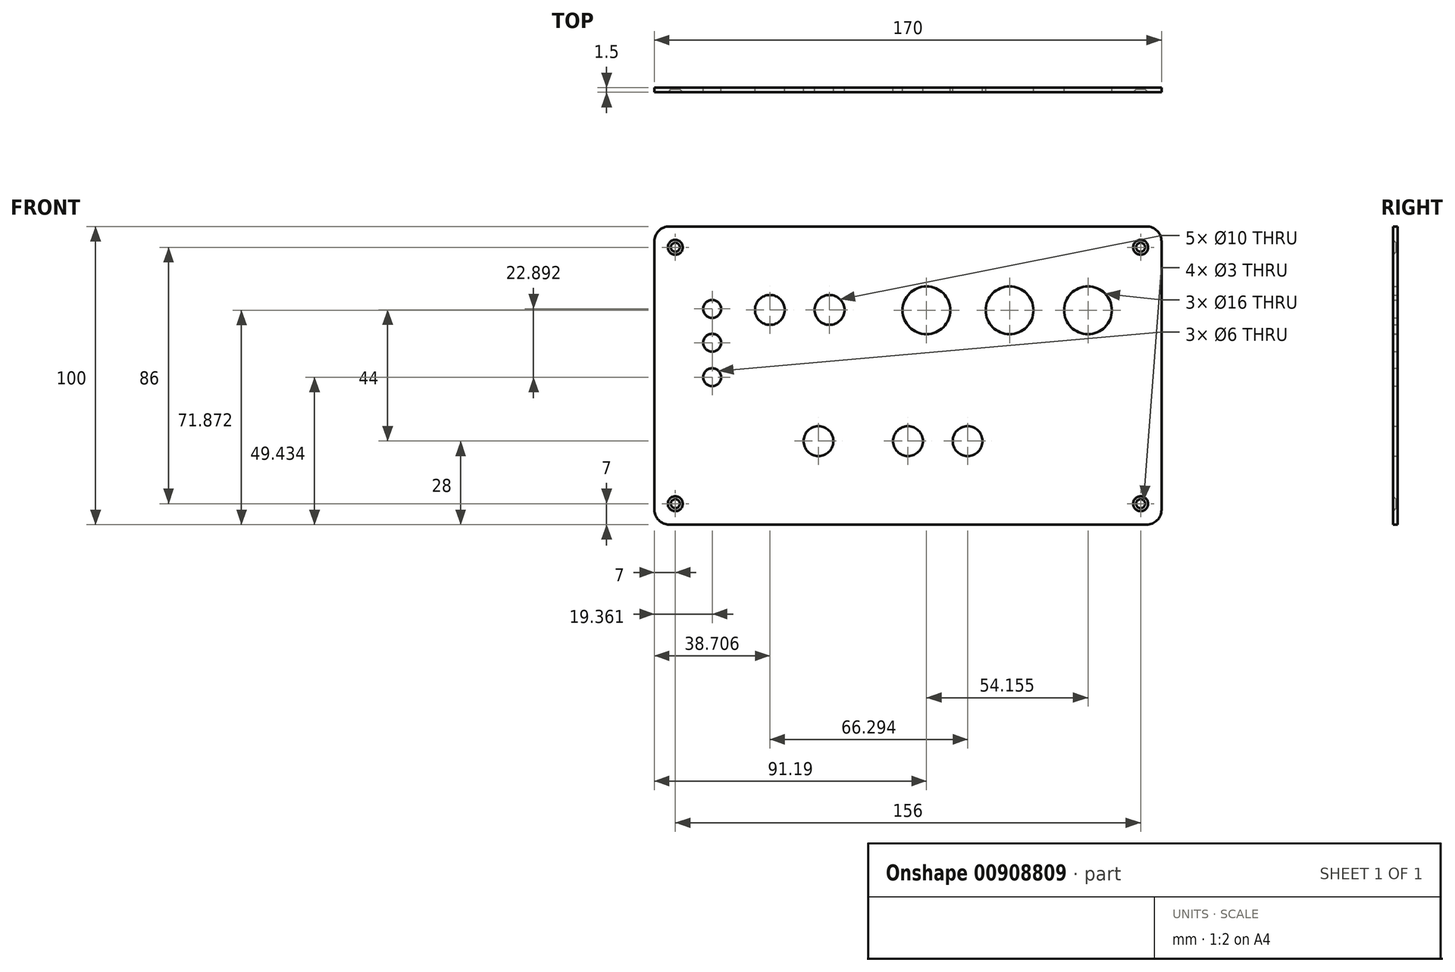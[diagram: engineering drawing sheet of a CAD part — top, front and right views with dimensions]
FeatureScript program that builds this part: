
annotation { "Feature Type Name" : "Feature", "Feature Type Description" : "" }
export const myFeature = defineFeature(function(context is Context, id is Id, definition is map)
    precondition{}
    {
        {
            var Q0;
            Q0=qCreatedBy(makeId("Front.planeOp"),FACE);
            var sketch = newSketch(context, id + "F0", { "sketchPlane" : qUnion([Q0])});
            skLineSegment(sketch, "E0.bottom", {"start": v(5, 0) * mm, "end": v(165, 0) * mm});
            skLineSegment(sketch, "E0.top", {"start": v(5, 100) * mm, "end": v(165, 100) * mm});
            skLineSegment(sketch, "E0.left", {"start": v(0, 5) * mm, "end": v(0, 95) * mm});
            skLineSegment(sketch, "E0.right", {"start": v(170, 5) * mm, "end": v(170, 95) * mm});
            skCircle(sketch, "E1", {"center": v(145.35, 71.87) * mm, "radius": 8 * mm});
            skPoint(sketch, "E2.visualSharp", {"position": v(0, 100) * mm});
            skArc(sketch, "E2.filletArc", {"start": v(5, 100) * mm, "mid": v(1.46, 98.54) * mm, "end": v(0, 95) * mm});
            skPoint(sketch, "E3.visualSharp", {"position": v(0, 0) * mm});
            skArc(sketch, "E3.filletArc", {"start": v(0, 5) * mm, "mid": v(1.46, 1.46) * mm, "end": v(5, 0) * mm});
            skPoint(sketch, "E4.visualSharp", {"position": v(170, 0) * mm});
            skArc(sketch, "E4.filletArc", {"start": v(165, 0) * mm, "mid": v(168.54, 1.46) * mm, "end": v(170, 5) * mm});
            skPoint(sketch, "E5.visualSharp", {"position": v(170, 100) * mm});
            skArc(sketch, "E5.filletArc", {"start": v(170, 95) * mm, "mid": v(168.54, 98.54) * mm, "end": v(165, 100) * mm});
            skLineSegment(sketch, "E6.bottom", {"start": v(163, 7) * mm, "end": v(7, 7) * mm, "construction": true});
            skLineSegment(sketch, "E6.top", {"start": v(163, 93) * mm, "end": v(7, 93) * mm, "construction": true});
            skLineSegment(sketch, "E6.left", {"start": v(163, 7) * mm, "end": v(163, 93) * mm, "construction": true});
            skLineSegment(sketch, "E6.right", {"start": v(7, 7) * mm, "end": v(7, 93) * mm, "construction": true});
            skCircle(sketch, "E7", {"center": v(7, 7) * mm, "radius": 1.5 * mm});
            skCircle(sketch, "E8", {"center": v(163, 93) * mm, "radius": 1.5 * mm});
            skCircle(sketch, "E9", {"center": v(163, 7) * mm, "radius": 1.5 * mm});
            skCircle(sketch, "E10", {"center": v(7, 93) * mm, "radius": 1.5 * mm});
            skCircle(sketch, "E11", {"center": v(105, 28) * mm, "radius": 5 * mm});
            skCircle(sketch, "E12", {"center": v(91.2, 71.87) * mm, "radius": 8 * mm});
            skCircle(sketch, "E13", {"center": v(85, 28) * mm, "radius": 5 * mm});
            skCircle(sketch, "E14", {"center": v(119.06, 71.87) * mm, "radius": 8 * mm});
            skCircle(sketch, "E15", {"center": v(55, 28) * mm, "radius": 5 * mm});
            skLineSegment(sketch, "E16", {"start": v(12.83, 28) * mm, "end": v(149.09, 28) * mm, "construction": true});
            skPoint(sketch, "E17", {"position": v(85, 0) * mm});
            skPoint(sketch, "E18", {"position": v(85, 100) * mm});
            skCircle(sketch, "E19", {"center": v(19.36, 49.43) * mm, "radius": 3 * mm});
            skCircle(sketch, "E20", {"center": v(38.7, 72) * mm, "radius": 5 * mm});
            skCircle(sketch, "E21", {"center": v(58.7, 72) * mm, "radius": 5 * mm});
            skCircle(sketch, "E22", {"center": v(19.36, 61) * mm, "radius": 3 * mm});
            skLineSegment(sketch, "E23", {"start": v(38.7, 72) * mm, "end": v(58.7, 72) * mm, "construction": true});
            skCircle(sketch, "E24", {"center": v(19.36, 72.33) * mm, "radius": 3 * mm});
            skSolve(sketch);
        }
        {
            var Q0;
            Q0=qSketchRegion(id+"F0",true);
            extrude(context, id + "F1", {"entities" : qUnion([Q0]), "depth" : 1.5 * mm});
        }
        {
            var Q0;
            Q0=makeQuery(id+"F1.opExtrude","CAP_EDGE",EDGE,{"disambiguationData":[OSD([sQuery(id+"F0.wireOp",EDGE,"E8")])],"isStart":false});
            var Q1;
            Q1=makeQuery(id+"F1.opExtrude","CAP_EDGE",EDGE,{"disambiguationData":[OSD([sQuery(id+"F0.wireOp",EDGE,"E9")])],"isStart":false});
            var Q2;
            Q2=makeQuery(id+"F1.opExtrude","CAP_EDGE",EDGE,{"disambiguationData":[OSD([sQuery(id+"F0.wireOp",EDGE,"E10")])],"isStart":false});
            var Q3;
            Q3=makeQuery(id+"F1.opExtrude","CAP_EDGE",EDGE,{"disambiguationData":[OSD([sQuery(id+"F0.wireOp",EDGE,"E7")])],"isStart":false});
            chamfer(context, id + "F2", {"entities" : qUnion([Q0, Q1, Q2, Q3]), "width" : 1 * mm, "tangentPropagation" : true});
        }
    });
